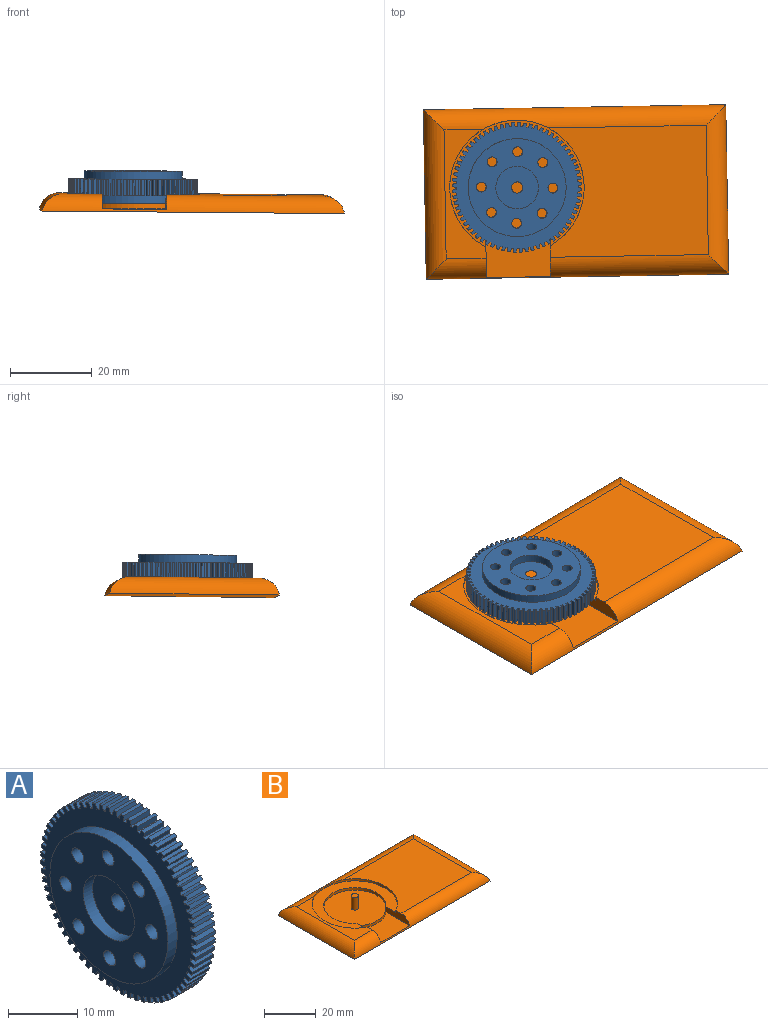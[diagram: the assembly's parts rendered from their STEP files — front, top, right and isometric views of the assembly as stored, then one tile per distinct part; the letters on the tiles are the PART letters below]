
ASSEMBLY  parts=2 mates=1
PART A: 292 faces, bbox 7.8x31.7x31.7 mm
  f0: cylinder r=1.22mm len=7.79mm, axis (1,0,0), area 59.7mm2, adj f277,f284
  f1: cylinder r=1.22mm len=7.79mm, axis (1,0,0), area 59.7mm2, adj f277,f284
  f2: cylinder r=1.22mm len=7.79mm, axis (1,0,0), area 59.7mm2, adj f277,f284
  f3: cylinder r=1.22mm len=7.79mm, axis (1,0,0), area 59.7mm2, adj f277,f284
  f4: cylinder r=1.22mm len=7.79mm, axis (1,0,0), area 59.7mm2, adj f277,f284
  f5: cylinder r=1.22mm len=7.79mm, axis (1,0,0), area 59.7mm2, adj f277,f284
  f6: cylinder r=1.22mm len=7.79mm, axis (1,0,0), area 59.7mm2, adj f277,f284
  f7: cylinder r=15.86mm len=3.95mm, axis (-1,0,0), area 2.5mm2, adj f10,f13,f276,f286
  f8: plane 3.95x0.5mm, normal (0,0.08,1), area 2mm2, adj f9,f10,f276,f286
  f9: plane 3.95x0.9mm, normal (0,0.99,0.12), area 3.6mm2, adj f8,f275,f276,f286
  f10: plane 3.95x0.86mm, normal (0,-0.97,0.26), area 3.5mm2, adj f7,f8,f276,f286
  f11: cylinder r=15.86mm len=3.95mm, axis (-1,0,0), area 2.5mm2, adj f14,f17,f276,f286
  f12: plane 3.95x0.49mm, normal (0,0.17,0.98), area 2mm2, adj f13,f14,f276,f286
  f13: plane 3.95x0.9mm, normal (0,1,0.03), area 3.6mm2, adj f7,f12,f276,f286
  f14: plane 3.95x0.84mm, normal (0,-0.94,0.35), area 3.5mm2, adj f11,f12,f276,f286
  f15: cylinder r=15.86mm len=3.95mm, axis (-1,0,0), area 2.5mm2, adj f18,f21,f276,f286
  f16: plane 3.95x0.48mm, normal (0,0.26,0.96), area 2mm2, adj f17,f18,f276,f286
  f17: plane 3.95x0.9mm, normal (0,1,-0.06), area 3.6mm2, adj f11,f16,f276,f286
  f18: plane 3.95x0.8mm, normal (0,-0.9,0.43), area 3.5mm2, adj f15,f16,f276,f286
  f19: cylinder r=15.86mm len=3.95mm, axis (-1,0,0), area 2.5mm2, adj f22,f25,f276,f286
  f20: plane 3.95x0.47mm, normal (0,0.35,0.94), area 2mm2, adj f21,f22,f276,f286
  f21: plane 3.95x0.89mm, normal (0,0.99,-0.15), area 3.6mm2, adj f15,f20,f276,f286
  f22: plane 3.95x0.77mm, normal (0,-0.86,0.51), area 3.5mm2, adj f19,f20,f276,f286
  f23: cylinder r=15.86mm len=3.95mm, axis (-1,0,0), area 2.5mm2, adj f26,f29,f276,f286
  f24: plane 3.95x0.45mm, normal (0,0.44,0.9), area 2mm2, adj f25,f26,f276,f286
  f25: plane 3.95x0.88mm, normal (0,0.97,-0.24), area 3.6mm2, adj f19,f24,f276,f286
  f26: plane 3.95x0.72mm, normal (0,-0.81,0.59), area 3.5mm2, adj f23,f24,f276,f286
  f27: cylinder r=15.86mm len=3.95mm, axis (-1,0,0), area 2.5mm2, adj f30,f33,f276,f286
  f28: plane 3.95x0.43mm, normal (0,0.52,0.86), area 2mm2, adj f29,f30,f276,f286
  f29: plane 3.95x0.85mm, normal (0,0.94,-0.33), area 3.6mm2, adj f23,f28,f276,f286
  f30: plane 3.95x0.67mm, normal (0,-0.75,0.66), area 3.5mm2, adj f27,f28,f276,f286
  f31: cylinder r=15.86mm len=3.95mm, axis (-1,0,0), area 2.5mm2, adj f34,f37,f276,f286
  f32: plane 3.95x0.4mm, normal (0,0.59,0.8), area 2mm2, adj f33,f34,f276,f286
  f33: plane 3.95x0.82mm, normal (0,0.91,-0.42), area 3.6mm2, adj f27,f32,f276,f286
  f34: plane 3.95x0.65mm, normal (0,-0.69,0.73), area 3.5mm2, adj f31,f32,f276,f286
  f35: cylinder r=15.86mm len=3.95mm, axis (-1,0,0), area 2.5mm2, adj f38,f41,f276,f286
  f36: plane 3.95x0.37mm, normal (0,0.67,0.75), area 2mm2, adj f37,f38,f276,f286
  f37: plane 3.95x0.78mm, normal (0,0.87,-0.5), area 3.6mm2, adj f31,f36,f276,f286
  f38: plane 3.95x0.7mm, normal (0,-0.62,0.79), area 3.5mm2, adj f35,f36,f276,f286
  f39: cylinder r=15.86mm len=3.95mm, axis (-1,0,0), area 2.5mm2, adj f42,f45,f276,f286
  f40: plane 3.95x0.36mm, normal (0,0.73,0.68), area 2mm2, adj f41,f42,f276,f286
  f41: plane 3.95x0.74mm, normal (0,0.82,-0.58), area 3.6mm2, adj f35,f40,f276,f286
  f42: plane 3.95x0.75mm, normal (0,-0.54,0.84), area 3.5mm2, adj f39,f40,f276,f286
  f43: cylinder r=15.86mm len=3.95mm, axis (-1,0,0), area 2.5mm2, adj f46,f49,f276,f286
  f44: plane 3.95x0.39mm, normal (0,0.79,0.61), area 2mm2, adj f45,f46,f276,f286
  f45: plane 3.95x0.69mm, normal (0,0.76,-0.65), area 3.6mm2, adj f39,f44,f276,f286
  f46: plane 3.95x0.79mm, normal (0,-0.46,0.89), area 3.5mm2, adj f43,f44,f276,f286
  f47: cylinder r=15.86mm len=3.95mm, axis (-1,0,0), area 2.5mm2, adj f50,f53,f276,f286
  f48: plane 3.95x0.42mm, normal (0,0.84,0.54), area 2mm2, adj f49,f50,f276,f286
  f49: plane 3.95x0.65mm, normal (0,0.7,-0.72), area 3.6mm2, adj f43,f48,f276,f286
  f50: plane 3.95x0.83mm, normal (0,-0.38,0.93), area 3.5mm2, adj f47,f48,f276,f286
  f51: cylinder r=15.86mm len=3.95mm, axis (-1,0,0), area 2.5mm2, adj f54,f57,f276,f286
  f52: plane 3.95x0.44mm, normal (0,0.89,0.46), area 2mm2, adj f53,f54,f276,f286
  f53: plane 3.95x0.7mm, normal (0,0.63,-0.78), area 3.6mm2, adj f47,f52,f276,f286
  f54: plane 3.95x0.85mm, normal (0,-0.29,0.96), area 3.5mm2, adj f51,f52,f276,f286
  f55: cylinder r=15.86mm len=3.95mm, axis (-1,0,0), area 2.5mm2, adj f58,f61,f276,f286
  f56: plane 3.95x0.46mm, normal (0,0.93,0.37), area 2mm2, adj f57,f58,f276,f286
  f57: plane 3.95x0.75mm, normal (0,0.55,-0.83), area 3.6mm2, adj f51,f56,f276,f286
  f58: plane 3.95x0.87mm, normal (0,-0.2,0.98), area 3.5mm2, adj f55,f56,f276,f286
  f59: cylinder r=15.86mm len=3.95mm, axis (-1,0,0), area 2.5mm2, adj f62,f65,f276,f286
  f60: plane 3.95x0.48mm, normal (0,0.96,0.28), area 2mm2, adj f61,f62,f276,f286
  f61: plane 3.95x0.8mm, normal (0,0.47,-0.88), area 3.6mm2, adj f55,f60,f276,f286
  f62: plane 3.95x0.89mm, normal (0,-0.11,0.99), area 3.5mm2, adj f59,f60,f276,f286
  f63: cylinder r=15.86mm len=3.95mm, axis (-1,0,0), area 2.5mm2, adj f66,f69,f276,f286
  f64: plane 3.95x0.49mm, normal (0,0.98,0.19), area 2mm2, adj f65,f66,f276,f286
  f65: plane 3.95x0.83mm, normal (0,0.39,-0.92), area 3.6mm2, adj f59,f64,f276,f286
  f66: plane 3.95x0.89mm, normal (0,-0.02,1), area 3.5mm2, adj f63,f64,f276,f286
  f67: cylinder r=15.86mm len=3.95mm, axis (-1,0,0), area 2.5mm2, adj f70,f73,f276,f286
  f68: plane 3.95x0.49mm, normal (0,0.99,0.1), area 2mm2, adj f69,f70,f276,f286
  f69: plane 3.95x0.86mm, normal (0,0.3,-0.95), area 3.6mm2, adj f63,f68,f276,f286
  f70: plane 3.95x0.89mm, normal (0,0.08,1), area 3.5mm2, adj f67,f68,f276,f286
  f71: cylinder r=15.86mm len=3.95mm, axis (-1,0,0), area 2.5mm2, adj f74,f77,f276,f286
  f72: plane 3.95x0.5mm, normal (0,1,0.01), area 2mm2, adj f73,f74,f276,f286
  f73: plane 3.95x0.88mm, normal (0,0.22,-0.98), area 3.6mm2, adj f67,f72,f276,f286
  f74: plane 3.95x0.88mm, normal (0,0.17,0.99), area 3.5mm2, adj f71,f72,f276,f286
  f75: cylinder r=15.86mm len=3.95mm, axis (-1,0,0), area 2.5mm2, adj f78,f81,f276,f286
  f76: plane 3.95x0.5mm, normal (0,1,-0.08), area 2mm2, adj f77,f78,f276,f286
  f77: plane 3.95x0.9mm, normal (0,0.12,-0.99), area 3.6mm2, adj f71,f76,f276,f286
  f78: plane 3.95x0.86mm, normal (0,0.26,0.97), area 3.5mm2, adj f75,f76,f276,f286
  f79: cylinder r=15.86mm len=3.95mm, axis (-1,0,0), area 2.5mm2, adj f82,f85,f276,f286
  f80: plane 3.95x0.49mm, normal (0,0.98,-0.17), area 2mm2, adj f81,f82,f276,f286
  f81: plane 3.95x0.9mm, normal (0,0.03,-1), area 3.6mm2, adj f75,f80,f276,f286
  f82: plane 3.95x0.84mm, normal (0,0.35,0.94), area 3.5mm2, adj f79,f80,f276,f286
  f83: cylinder r=15.86mm len=3.95mm, axis (-1,0,0), area 2.5mm2, adj f86,f89,f276,f286
  f84: plane 3.95x0.48mm, normal (0,0.96,-0.26), area 2mm2, adj f85,f86,f276,f286
  f85: plane 3.95x0.9mm, normal (0,-0.06,-1), area 3.6mm2, adj f79,f84,f276,f286
  f86: plane 3.95x0.8mm, normal (0,0.43,0.9), area 3.5mm2, adj f83,f84,f276,f286
  f87: cylinder r=15.86mm len=3.95mm, axis (-1,0,0), area 2.5mm2, adj f90,f93,f276,f286
  f88: plane 3.95x0.47mm, normal (0,0.94,-0.35), area 2mm2, adj f89,f90,f276,f286
  f89: plane 3.95x0.89mm, normal (0,-0.15,-0.99), area 3.6mm2, adj f83,f88,f276,f286
  f90: plane 3.95x0.77mm, normal (0,0.51,0.86), area 3.5mm2, adj f87,f88,f276,f286
  f91: cylinder r=15.86mm len=3.95mm, axis (-1,0,0), area 2.5mm2, adj f94,f97,f276,f286
  f92: plane 3.95x0.45mm, normal (0,0.9,-0.44), area 2mm2, adj f93,f94,f276,f286
  f93: plane 3.95x0.88mm, normal (0,-0.24,-0.97), area 3.6mm2, adj f87,f92,f276,f286
  f94: plane 3.95x0.72mm, normal (0,0.59,0.81), area 3.5mm2, adj f91,f92,f276,f286
  f95: cylinder r=15.86mm len=3.95mm, axis (-1,0,0), area 2.5mm2, adj f98,f101,f276,f286
  f96: plane 3.95x0.43mm, normal (0,0.86,-0.52), area 2mm2, adj f97,f98,f276,f286
  f97: plane 3.95x0.85mm, normal (0,-0.33,-0.94), area 3.6mm2, adj f91,f96,f276,f286
  f98: plane 3.95x0.67mm, normal (0,0.66,0.75), area 3.5mm2, adj f95,f96,f276,f286
  f99: cylinder r=15.86mm len=3.95mm, axis (-1,0,0), area 2.5mm2, adj f102,f105,f276,f286
  f100: plane 3.95x0.4mm, normal (0,0.8,-0.59), area 2mm2, adj f101,f102,f276,f286
  f101: plane 3.95x0.82mm, normal (0,-0.42,-0.91), area 3.6mm2, adj f95,f100,f276,f286
  f102: plane 3.95x0.65mm, normal (0,0.73,0.69), area 3.5mm2, adj f99,f100,f276,f286
  f103: cylinder r=15.86mm len=3.95mm, axis (-1,0,0), area 2.5mm2, adj f106,f109,f276,f286
  f104: plane 3.95x0.37mm, normal (0,0.75,-0.67), area 2mm2, adj f105,f106,f276,f286
  f105: plane 3.95x0.78mm, normal (0,-0.5,-0.87), area 3.6mm2, adj f99,f104,f276,f286
  f106: plane 3.95x0.7mm, normal (0,0.79,0.62), area 3.5mm2, adj f103,f104,f276,f286
  f107: cylinder r=15.86mm len=3.95mm, axis (-1,0,0), area 2.5mm2, adj f110,f113,f276,f286
  f108: plane 3.95x0.36mm, normal (0,0.68,-0.73), area 2mm2, adj f109,f110,f276,f286
  f109: plane 3.95x0.74mm, normal (0,-0.58,-0.82), area 3.6mm2, adj f103,f108,f276,f286
  f110: plane 3.95x0.75mm, normal (0,0.84,0.54), area 3.5mm2, adj f107,f108,f276,f286
  f111: cylinder r=15.86mm len=3.95mm, axis (-1,0,0), area 2.5mm2, adj f114,f117,f276,f286
  f112: plane 3.95x0.39mm, normal (0,0.61,-0.79), area 2mm2, adj f113,f114,f276,f286
  f113: plane 3.95x0.69mm, normal (0,-0.65,-0.76), area 3.6mm2, adj f107,f112,f276,f286
  f114: plane 3.95x0.79mm, normal (0,0.89,0.46), area 3.5mm2, adj f111,f112,f276,f286
  f115: cylinder r=15.86mm len=3.95mm, axis (-1,0,0), area 2.5mm2, adj f118,f121,f276,f286
  f116: plane 3.95x0.42mm, normal (0,0.54,-0.84), area 2mm2, adj f117,f118,f276,f286
  f117: plane 3.95x0.65mm, normal (0,-0.72,-0.7), area 3.6mm2, adj f111,f116,f276,f286
  f118: plane 3.95x0.83mm, normal (0,0.93,0.38), area 3.5mm2, adj f115,f116,f276,f286
  f119: cylinder r=15.86mm len=3.95mm, axis (-1,0,0), area 2.5mm2, adj f122,f125,f276,f286
  f120: plane 3.95x0.44mm, normal (0,0.46,-0.89), area 2mm2, adj f121,f122,f276,f286
  f121: plane 3.95x0.7mm, normal (0,-0.78,-0.63), area 3.6mm2, adj f115,f120,f276,f286
  f122: plane 3.95x0.85mm, normal (0,0.96,0.29), area 3.5mm2, adj f119,f120,f276,f286
  f123: cylinder r=15.86mm len=3.95mm, axis (-1,0,0), area 2.5mm2, adj f126,f129,f276,f286
  f124: plane 3.95x0.46mm, normal (0,0.37,-0.93), area 2mm2, adj f125,f126,f276,f286
  f125: plane 3.95x0.75mm, normal (0,-0.83,-0.55), area 3.6mm2, adj f119,f124,f276,f286
  f126: plane 3.95x0.87mm, normal (0,0.98,0.2), area 3.5mm2, adj f123,f124,f276,f286
  f127: cylinder r=15.86mm len=3.95mm, axis (-1,0,0), area 2.5mm2, adj f130,f133,f276,f286
  f128: plane 3.95x0.48mm, normal (0,0.28,-0.96), area 2mm2, adj f129,f130,f276,f286
  f129: plane 3.95x0.8mm, normal (0,-0.88,-0.47), area 3.6mm2, adj f123,f128,f276,f286
  f130: plane 3.95x0.89mm, normal (0,0.99,0.11), area 3.5mm2, adj f127,f128,f276,f286
  f131: cylinder r=15.86mm len=3.95mm, axis (-1,0,0), area 2.5mm2, adj f134,f137,f276,f286
  f132: plane 3.95x0.49mm, normal (0,0.19,-0.98), area 2mm2, adj f133,f134,f276,f286
  f133: plane 3.95x0.83mm, normal (0,-0.92,-0.39), area 3.6mm2, adj f127,f132,f276,f286
  f134: plane 3.95x0.89mm, normal (0,1,0.02), area 3.5mm2, adj f131,f132,f276,f286
  f135: cylinder r=15.86mm len=3.95mm, axis (-1,0,0), area 2.5mm2, adj f138,f141,f276,f286
  f136: plane 3.95x0.49mm, normal (0,0.1,-0.99), area 2mm2, adj f137,f138,f276,f286
  f137: plane 3.95x0.86mm, normal (0,-0.95,-0.3), area 3.6mm2, adj f131,f136,f276,f286
  f138: plane 3.95x0.89mm, normal (0,1,-0.08), area 3.5mm2, adj f135,f136,f276,f286
  f139: cylinder r=15.86mm len=3.95mm, axis (-1,0,0), area 2.5mm2, adj f142,f145,f276,f286
  f140: plane 3.95x0.5mm, normal (0,0.01,-1), area 2mm2, adj f141,f142,f276,f286
  f141: plane 3.95x0.88mm, normal (0,-0.98,-0.22), area 3.6mm2, adj f135,f140,f276,f286
  f142: plane 3.95x0.88mm, normal (0,0.99,-0.17), area 3.5mm2, adj f139,f140,f276,f286
  f143: cylinder r=15.86mm len=3.95mm, axis (-1,0,0), area 2.5mm2, adj f146,f149,f276,f286
  f144: plane 3.95x0.5mm, normal (0,-0.08,-1), area 2mm2, adj f145,f146,f276,f286
  f145: plane 3.95x0.9mm, normal (0,-0.99,-0.12), area 3.6mm2, adj f139,f144,f276,f286
  f146: plane 3.95x0.86mm, normal (0,0.97,-0.26), area 3.5mm2, adj f143,f144,f276,f286
  f147: cylinder r=15.86mm len=3.95mm, axis (-1,0,0), area 2.5mm2, adj f150,f153,f276,f286
  f148: plane 3.95x0.49mm, normal (0,-0.17,-0.98), area 2mm2, adj f149,f150,f276,f286
  f149: plane 3.95x0.9mm, normal (0,-1,-0.03), area 3.6mm2, adj f143,f148,f276,f286
  f150: plane 3.95x0.84mm, normal (0,0.94,-0.35), area 3.5mm2, adj f147,f148,f276,f286
  f151: cylinder r=15.86mm len=3.95mm, axis (-1,0,0), area 2.5mm2, adj f154,f157,f276,f286
  f152: plane 3.95x0.48mm, normal (0,-0.26,-0.96), area 2mm2, adj f153,f154,f276,f286
  f153: plane 3.95x0.9mm, normal (0,-1,0.06), area 3.6mm2, adj f147,f152,f276,f286
  f154: plane 3.95x0.8mm, normal (0,0.9,-0.43), area 3.5mm2, adj f151,f152,f276,f286
  f155: cylinder r=15.86mm len=3.95mm, axis (-1,0,0), area 2.5mm2, adj f158,f161,f276,f286
  f156: plane 3.95x0.47mm, normal (0,-0.35,-0.94), area 2mm2, adj f157,f158,f276,f286
  f157: plane 3.95x0.89mm, normal (0,-0.99,0.15), area 3.6mm2, adj f151,f156,f276,f286
  f158: plane 3.95x0.77mm, normal (0,0.86,-0.51), area 3.5mm2, adj f155,f156,f276,f286
  f159: cylinder r=15.86mm len=3.95mm, axis (-1,0,0), area 2.5mm2, adj f162,f165,f276,f286
  f160: plane 3.95x0.45mm, normal (0,-0.44,-0.9), area 2mm2, adj f161,f162,f276,f286
  f161: plane 3.95x0.88mm, normal (0,-0.97,0.24), area 3.6mm2, adj f155,f160,f276,f286
  f162: plane 3.95x0.72mm, normal (0,0.81,-0.59), area 3.5mm2, adj f159,f160,f276,f286
  f163: cylinder r=15.86mm len=3.95mm, axis (-1,0,0), area 2.5mm2, adj f166,f169,f276,f286
  f164: plane 3.95x0.43mm, normal (0,-0.52,-0.86), area 2mm2, adj f165,f166,f276,f286
  f165: plane 3.95x0.85mm, normal (0,-0.94,0.33), area 3.6mm2, adj f159,f164,f276,f286
  f166: plane 3.95x0.67mm, normal (0,0.75,-0.66), area 3.5mm2, adj f163,f164,f276,f286
  f167: cylinder r=15.86mm len=3.95mm, axis (-1,0,0), area 2.5mm2, adj f170,f173,f276,f286
  f168: plane 3.95x0.4mm, normal (0,-0.59,-0.8), area 2mm2, adj f169,f170,f276,f286
  f169: plane 3.95x0.82mm, normal (0,-0.91,0.42), area 3.6mm2, adj f163,f168,f276,f286
  f170: plane 3.95x0.65mm, normal (0,0.69,-0.73), area 3.5mm2, adj f167,f168,f276,f286
  f171: cylinder r=15.86mm len=3.95mm, axis (-1,0,0), area 2.5mm2, adj f174,f177,f276,f286
  f172: plane 3.95x0.37mm, normal (0,-0.67,-0.75), area 2mm2, adj f173,f174,f276,f286
  f173: plane 3.95x0.78mm, normal (0,-0.87,0.5), area 3.6mm2, adj f167,f172,f276,f286
  f174: plane 3.95x0.7mm, normal (0,0.62,-0.79), area 3.5mm2, adj f171,f172,f276,f286
  f175: cylinder r=15.86mm len=3.95mm, axis (-1,0,0), area 2.5mm2, adj f178,f181,f276,f286
  f176: plane 3.95x0.36mm, normal (0,-0.73,-0.68), area 2mm2, adj f177,f178,f276,f286
  f177: plane 3.95x0.74mm, normal (0,-0.82,0.58), area 3.6mm2, adj f171,f176,f276,f286
  f178: plane 3.95x0.75mm, normal (0,0.54,-0.84), area 3.5mm2, adj f175,f176,f276,f286
  f179: cylinder r=15.86mm len=3.95mm, axis (-1,0,0), area 2.5mm2, adj f182,f185,f276,f286
  f180: plane 3.95x0.39mm, normal (0,-0.79,-0.61), area 2mm2, adj f181,f182,f276,f286
  f181: plane 3.95x0.69mm, normal (0,-0.76,0.65), area 3.6mm2, adj f175,f180,f276,f286
  f182: plane 3.95x0.79mm, normal (0,0.46,-0.89), area 3.5mm2, adj f179,f180,f276,f286
  f183: cylinder r=15.86mm len=3.95mm, axis (-1,0,0), area 2.5mm2, adj f186,f189,f276,f286
  f184: plane 3.95x0.42mm, normal (0,-0.84,-0.54), area 2mm2, adj f185,f186,f276,f286
  f185: plane 3.95x0.65mm, normal (0,-0.7,0.72), area 3.6mm2, adj f179,f184,f276,f286
  f186: plane 3.95x0.83mm, normal (0,0.38,-0.93), area 3.5mm2, adj f183,f184,f276,f286
  f187: cylinder r=15.86mm len=3.95mm, axis (-1,0,0), area 2.5mm2, adj f190,f193,f276,f286
  f188: plane 3.95x0.44mm, normal (0,-0.89,-0.46), area 2mm2, adj f189,f190,f276,f286
  f189: plane 3.95x0.7mm, normal (0,-0.63,0.78), area 3.6mm2, adj f183,f188,f276,f286
  f190: plane 3.95x0.85mm, normal (0,0.29,-0.96), area 3.5mm2, adj f187,f188,f276,f286
  f191: cylinder r=15.86mm len=3.95mm, axis (-1,0,0), area 2.5mm2, adj f194,f197,f276,f286
  f192: plane 3.95x0.46mm, normal (0,-0.93,-0.37), area 2mm2, adj f193,f194,f276,f286
  f193: plane 3.95x0.75mm, normal (0,-0.55,0.83), area 3.6mm2, adj f187,f192,f276,f286
  f194: plane 3.95x0.87mm, normal (0,0.2,-0.98), area 3.5mm2, adj f191,f192,f276,f286
  f195: cylinder r=15.86mm len=3.95mm, axis (-1,0,0), area 2.5mm2, adj f198,f201,f276,f286
  f196: plane 3.95x0.48mm, normal (0,-0.96,-0.28), area 2mm2, adj f197,f198,f276,f286
  f197: plane 3.95x0.8mm, normal (0,-0.47,0.88), area 3.6mm2, adj f191,f196,f276,f286
  f198: plane 3.95x0.89mm, normal (0,0.11,-0.99), area 3.5mm2, adj f195,f196,f276,f286
  f199: cylinder r=15.86mm len=3.95mm, axis (-1,0,0), area 2.5mm2, adj f202,f205,f276,f286
  f200: plane 3.95x0.49mm, normal (0,-0.98,-0.19), area 2mm2, adj f201,f202,f276,f286
  f201: plane 3.95x0.83mm, normal (0,-0.39,0.92), area 3.6mm2, adj f195,f200,f276,f286
  f202: plane 3.95x0.89mm, normal (0,0.02,-1), area 3.5mm2, adj f199,f200,f276,f286
  f203: cylinder r=15.86mm len=3.95mm, axis (-1,0,0), area 2.5mm2, adj f206,f209,f276,f286
  f204: plane 3.95x0.49mm, normal (0,-0.99,-0.1), area 2mm2, adj f205,f206,f276,f286
  f205: plane 3.95x0.86mm, normal (0,-0.3,0.95), area 3.6mm2, adj f199,f204,f276,f286
  f206: plane 3.95x0.89mm, normal (0,-0.08,-1), area 3.5mm2, adj f203,f204,f276,f286
  f207: cylinder r=15.86mm len=3.95mm, axis (-1,0,0), area 2.5mm2, adj f210,f213,f276,f286
  f208: plane 3.95x0.5mm, normal (0,-1,-0.01), area 2mm2, adj f209,f210,f276,f286
  f209: plane 3.95x0.88mm, normal (0,-0.22,0.98), area 3.6mm2, adj f203,f208,f276,f286
  f210: plane 3.95x0.88mm, normal (0,-0.17,-0.99), area 3.5mm2, adj f207,f208,f276,f286
  f211: cylinder r=15.86mm len=3.95mm, axis (-1,0,0), area 2.5mm2, adj f214,f217,f276,f286
  f212: plane 3.95x0.5mm, normal (0,-1,0.08), area 2mm2, adj f213,f214,f276,f286
  f213: plane 3.95x0.9mm, normal (0,-0.12,0.99), area 3.6mm2, adj f207,f212,f276,f286
  f214: plane 3.95x0.86mm, normal (0,-0.26,-0.97), area 3.5mm2, adj f211,f212,f276,f286
  f215: cylinder r=15.86mm len=3.95mm, axis (-1,0,0), area 2.5mm2, adj f218,f221,f276,f286
  f216: plane 3.95x0.49mm, normal (0,-0.98,0.17), area 2mm2, adj f217,f218,f276,f286
  f217: plane 3.95x0.9mm, normal (0,-0.03,1), area 3.6mm2, adj f211,f216,f276,f286
  f218: plane 3.95x0.84mm, normal (0,-0.35,-0.94), area 3.5mm2, adj f215,f216,f276,f286
  f219: cylinder r=15.86mm len=3.95mm, axis (-1,0,0), area 2.5mm2, adj f222,f225,f276,f286
  f220: plane 3.95x0.48mm, normal (0,-0.96,0.26), area 2mm2, adj f221,f222,f276,f286
  f221: plane 3.95x0.9mm, normal (0,0.06,1), area 3.6mm2, adj f215,f220,f276,f286
  f222: plane 3.95x0.8mm, normal (0,-0.43,-0.9), area 3.5mm2, adj f219,f220,f276,f286
  f223: cylinder r=15.86mm len=3.95mm, axis (-1,0,0), area 2.5mm2, adj f226,f229,f276,f286
  f224: plane 3.95x0.47mm, normal (0,-0.94,0.35), area 2mm2, adj f225,f226,f276,f286
  f225: plane 3.95x0.89mm, normal (0,0.15,0.99), area 3.6mm2, adj f219,f224,f276,f286
  f226: plane 3.95x0.77mm, normal (0,-0.51,-0.86), area 3.5mm2, adj f223,f224,f276,f286
  f227: cylinder r=15.86mm len=3.95mm, axis (-1,0,0), area 2.5mm2, adj f230,f233,f276,f286
  f228: plane 3.95x0.45mm, normal (0,-0.9,0.44), area 2mm2, adj f229,f230,f276,f286
  f229: plane 3.95x0.88mm, normal (0,0.24,0.97), area 3.6mm2, adj f223,f228,f276,f286
  f230: plane 3.95x0.72mm, normal (0,-0.59,-0.81), area 3.5mm2, adj f227,f228,f276,f286
  f231: cylinder r=15.86mm len=3.95mm, axis (-1,0,0), area 2.5mm2, adj f234,f237,f276,f286
  f232: plane 3.95x0.43mm, normal (0,-0.86,0.52), area 2mm2, adj f233,f234,f276,f286
  f233: plane 3.95x0.85mm, normal (0,0.33,0.94), area 3.6mm2, adj f227,f232,f276,f286
  f234: plane 3.95x0.67mm, normal (0,-0.66,-0.75), area 3.5mm2, adj f231,f232,f276,f286
  f235: cylinder r=15.86mm len=3.95mm, axis (-1,0,0), area 2.5mm2, adj f238,f241,f276,f286
  f236: plane 3.95x0.4mm, normal (0,-0.8,0.59), area 2mm2, adj f237,f238,f276,f286
  f237: plane 3.95x0.82mm, normal (0,0.42,0.91), area 3.6mm2, adj f231,f236,f276,f286
  f238: plane 3.95x0.65mm, normal (0,-0.73,-0.69), area 3.5mm2, adj f235,f236,f276,f286
  f239: cylinder r=15.86mm len=3.95mm, axis (-1,0,0), area 2.5mm2, adj f242,f245,f276,f286
  f240: plane 3.95x0.37mm, normal (0,-0.75,0.67), area 2mm2, adj f241,f242,f276,f286
  f241: plane 3.95x0.78mm, normal (0,0.5,0.87), area 3.6mm2, adj f235,f240,f276,f286
  f242: plane 3.95x0.7mm, normal (0,-0.79,-0.62), area 3.5mm2, adj f239,f240,f276,f286
  f243: cylinder r=15.86mm len=3.95mm, axis (-1,0,0), area 2.5mm2, adj f246,f249,f276,f286
  f244: plane 3.95x0.36mm, normal (0,-0.68,0.73), area 2mm2, adj f245,f246,f276,f286
  f245: plane 3.95x0.74mm, normal (0,0.58,0.82), area 3.6mm2, adj f239,f244,f276,f286
  f246: plane 3.95x0.75mm, normal (0,-0.84,-0.54), area 3.5mm2, adj f243,f244,f276,f286
  f247: cylinder r=15.86mm len=3.95mm, axis (-1,0,0), area 2.5mm2, adj f250,f253,f276,f286
  f248: plane 3.95x0.39mm, normal (0,-0.61,0.79), area 2mm2, adj f249,f250,f276,f286
  f249: plane 3.95x0.69mm, normal (0,0.65,0.76), area 3.6mm2, adj f243,f248,f276,f286
  f250: plane 3.95x0.79mm, normal (0,-0.89,-0.46), area 3.5mm2, adj f247,f248,f276,f286
  f251: cylinder r=15.86mm len=3.95mm, axis (-1,0,0), area 2.5mm2, adj f254,f257,f276,f286
  f252: plane 3.95x0.42mm, normal (0,-0.54,0.84), area 2mm2, adj f253,f254,f276,f286
  f253: plane 3.95x0.65mm, normal (0,0.72,0.7), area 3.6mm2, adj f247,f252,f276,f286
  f254: plane 3.95x0.83mm, normal (0,-0.93,-0.38), area 3.5mm2, adj f251,f252,f276,f286
  f255: cylinder r=15.86mm len=3.95mm, axis (-1,0,0), area 2.5mm2, adj f258,f261,f276,f286
  f256: plane 3.95x0.44mm, normal (0,-0.46,0.89), area 2mm2, adj f257,f258,f276,f286
  f257: plane 3.95x0.7mm, normal (0,0.78,0.63), area 3.6mm2, adj f251,f256,f276,f286
  f258: plane 3.95x0.85mm, normal (0,-0.96,-0.29), area 3.5mm2, adj f255,f256,f276,f286
  f259: cylinder r=15.86mm len=3.95mm, axis (-1,0,0), area 2.5mm2, adj f262,f265,f276,f286
  f260: plane 3.95x0.46mm, normal (0,-0.37,0.93), area 2mm2, adj f261,f262,f276,f286
  f261: plane 3.95x0.75mm, normal (0,0.83,0.55), area 3.6mm2, adj f255,f260,f276,f286
  f262: plane 3.95x0.87mm, normal (0,-0.98,-0.2), area 3.5mm2, adj f259,f260,f276,f286
  f263: cylinder r=15.86mm len=3.95mm, axis (-1,0,0), area 2.5mm2, adj f266,f269,f276,f286
  f264: plane 3.95x0.48mm, normal (0,-0.28,0.96), area 2mm2, adj f265,f266,f276,f286
  f265: plane 3.95x0.8mm, normal (0,0.88,0.47), area 3.6mm2, adj f259,f264,f276,f286
  f266: plane 3.95x0.89mm, normal (0,-0.99,-0.11), area 3.5mm2, adj f263,f264,f276,f286
  f267: cylinder r=15.86mm len=3.95mm, axis (-1,0,0), area 2.5mm2, adj f270,f273,f276,f286
  f268: plane 3.95x0.49mm, normal (0,-0.19,0.98), area 2mm2, adj f269,f270,f276,f286
  f269: plane 3.95x0.83mm, normal (0,0.92,0.39), area 3.6mm2, adj f263,f268,f276,f286
  f270: plane 3.95x0.89mm, normal (0,-1,-0.02), area 3.5mm2, adj f267,f268,f276,f286
  f271: cylinder r=15.86mm len=3.95mm, axis (-1,0,0), area 2.5mm2, adj f274,f276,f286,f289
  f272: plane 3.95x0.49mm, normal (0,-0.1,0.99), area 2mm2, adj f273,f274,f276,f286
  f273: plane 3.95x0.86mm, normal (0,0.95,0.3), area 3.6mm2, adj f267,f272,f276,f286
  f274: plane 3.95x0.89mm, normal (0,-1,0.08), area 3.5mm2, adj f271,f272,f276,f286
  f275: cylinder r=15.86mm len=3.95mm, axis (-1,0,0), area 2.5mm2, adj f9,f276,f286,f290
  f276: plane 31.71x31.71mm, normal (-1,0,0), area 296.9mm2, adj f7,f8,f9,f10,f11,f12,f13,f14
  f277: plane 24.02x24.02mm, normal (-1,0,0), area 330.1mm2, adj f0,f1,f2,f3,f4,f5,f6,f278
  f278: cylinder r=5.22mm len=10.45mm, axis (-1,0,0), area 63.5mm2, adj f277,f279
  f279: plane 10.45x10.45mm, normal (-1,0,0), area 79.8mm2, adj f278,f280
  f280: cylinder r=1.37mm len=2.75mm, axis (-1,0,0), area 18.7mm2, adj f279,f281
  f281: cone r=1.37mm half-angle=0.3deg, axis (-1,0,0), area 13mm2, adj f280,f282
  f282: plane 10.53x10.53mm, normal (1,0,0), area 81.2mm2, adj f281,f283
  f283: cylinder r=5.26mm len=10.53mm, axis (-1,0,0), area 72.4mm2, adj f282,f284
  f284: plane 24.02x24.02mm, normal (1,0,0), area 328.9mm2, adj f0,f1,f2,f3,f4,f5,f6,f283
  f285: cylinder r=12.01mm len=24.02mm, axis (-1,0,0), area 143.7mm2, adj f284,f286
  f286: plane 31.71x31.71mm, normal (1,0,0), area 296.9mm2, adj f7,f8,f9,f10,f11,f12,f13,f14
  f287: cylinder r=12.01mm len=24.02mm, axis (-1,0,0), area 146mm2, adj f276,f277
  f288: plane 3.95x0.5mm, normal (0,-0.01,1), area 2mm2, adj f276,f286,f289,f290
  f289: plane 3.95x0.88mm, normal (0,0.98,0.22), area 3.6mm2, adj f271,f276,f286,f288
  f290: plane 3.95x0.88mm, normal (0,-0.99,0.17), area 3.5mm2, adj f275,f276,f286,f288
  f291: cylinder r=1.22mm len=7.79mm, axis (1,0,0), area 59.7mm2, adj f277,f284
PART B: 18 faces, bbox 74.2x41.6x7.8 mm
  f0: plane 31.72x9.8mm, normal (0,0,1), area 132.5mm2, adj f4,f6,f7,f14,f16
  f1: cylinder r=12.01mm len=24.02mm, axis (0,0,1), area 70mm2, adj f2,f9,f14,f17
  f2: plane 2.5x0.05mm, normal (0,-1,0), area 0.1mm2, adj f1,f12,f13,f15,f17
  f3: plane 38.75x31.72mm, normal (0,0,1), area 1051.9mm2, adj f4,f6,f8,f12,f16
  f4: cylinder r=5mm len=74.17mm, axis (1,0,0), area 391.3mm2, adj f0,f3,f5,f7,f8,f12,f14,f15
  f5: plane 74.17x41.57mm, normal (0,0,-1), area 3083mm2, adj f4,f6,f7,f8
  f6: cylinder r=5mm len=74.17mm, axis (1,0,0), area 468.4mm2, adj f0,f3,f5,f7,f8,f16
  f7: cylinder r=5mm len=41.57mm, axis (0,-1,0), area 263.2mm2, adj f0,f4,f5,f6
  f8: cylinder r=5mm len=41.57mm, axis (0,-1,0), area 263.2mm2, adj f3,f4,f5,f6
  f9: plane 24.02x24.02mm, normal (0,0,1), area 447.4mm2, adj f1,f11,f13
  f10: plane 2.73x2.73mm, normal (0,0,1), area 5.9mm2, adj f11
  f11: cylinder r=1.37mm len=5.87mm, axis (0,0,-1), area 50.3mm2, adj f9,f10
  f12: plane 12.96x3.5mm, normal (-1,0,0), area 35.5mm2, adj f2,f3,f4,f15,f16,f17
  f13: cylinder r=12.01mm len=15.72mm, axis (0,0,1), area 22.3mm2, adj f2,f9,f14,f15
  f14: plane 12.96x3.5mm, normal (1,0,0), area 35.5mm2, adj f0,f1,f4,f13,f15,f16,f17
  f15: plane 15.76x12.96mm, normal (0,0,1), area 172.8mm2, adj f2,f4,f12,f13,f14
  f16: cylinder r=16.5mm len=33mm, axis (0,0,1), area 83.4mm2, adj f0,f3,f6,f12,f14,f17
  f17: plane 33x31.01mm, normal (0,0,1), area 326.9mm2, adj f1,f2,f12,f14,f16
PLACE A rot(axis=(0.37,0.85,-0.36),99.7deg) t=(19.57,21.16,-21.33)mm
PLACE B rot(axis=(0.51,0.39,0.77),1.3deg) t=(24.81,30.21,-26.92)mm fixed
MATE revolute B.f11 <-> A.f7  axis (0.01,-0.01,1) through (11.37,29.89,-19)mm
